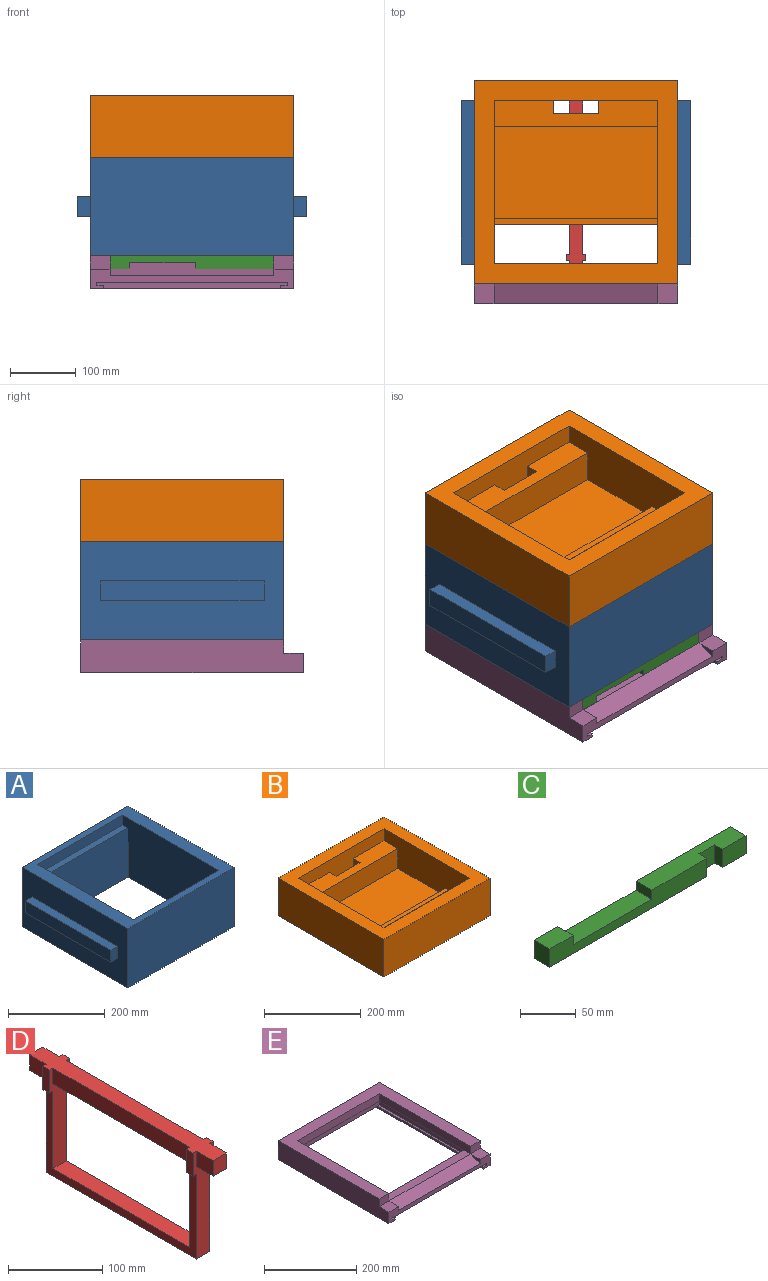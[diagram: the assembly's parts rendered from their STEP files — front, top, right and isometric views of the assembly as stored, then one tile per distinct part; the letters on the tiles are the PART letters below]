
ASSEMBLY  parts=5 mates=4
PART A: 24 faces, bbox 350x310x150 mm
  f0: plane 310x150mm, normal (1,0,0), area 39000mm2, adj f3,f4,f8,f9,f19,f20,f21,f22
  f1: plane 250x125mm, normal (0,1,0), area 31250mm2, adj f5,f6,f9,f12
  f2: plane 250x125mm, normal (0,-1,0), area 31250mm2, adj f5,f6,f9,f11
  f3: plane 310x150mm, normal (0,-1,0), area 46500mm2, adj f0,f7,f8,f9
  f4: plane 310x150mm, normal (0,1,0), area 46500mm2, adj f0,f7,f8,f9
  f5: plane 280x150mm, normal (-1,0,0), area 38250mm2, adj f1,f2,f8,f9,f10,f11,f12,f13
  f6: plane 280x150mm, normal (1,0,0), area 38250mm2, adj f1,f2,f8,f9,f10,f11,f12,f13
  f7: plane 310x150mm, normal (-1,0,0), area 39000mm2, adj f3,f4,f8,f9,f14,f15,f16,f17
  f8: plane 310x310mm, normal (0,0,1), area 26100mm2, adj f0,f3,f4,f5,f6,f7,f10,f13
  f9: plane 310x310mm, normal (0,0,-1), area 33600mm2, adj f0,f1,f2,f3,f4,f5,f6,f7
  f10: plane 250x25mm, normal (0,-1,0), area 6250mm2, adj f5,f6,f8,f11
  f11: plane 250x15mm, normal (0,0,1), area 3750mm2, adj f2,f5,f6,f10
  f12: plane 250x15mm, normal (0,0,1), area 3750mm2, adj f1,f5,f6,f13
  f13: plane 250x25mm, normal (0,1,0), area 6250mm2, adj f5,f6,f8,f12
  f14: plane 30x20mm, normal (0,-1,0), area 600mm2, adj f7,f15,f17,f18
  f15: plane 250x20mm, normal (0,0,1), area 5000mm2, adj f7,f14,f16,f18
  f16: plane 30x20mm, normal (0,1,0), area 600mm2, adj f7,f15,f17,f18
  f17: plane 250x20mm, normal (0,0,-1), area 5000mm2, adj f7,f14,f16,f18
  f18: plane 250x30mm, normal (-1,0,0), area 7500mm2, adj f14,f15,f16,f17
  f19: plane 30x20mm, normal (0,1,0), area 600mm2, adj f0,f20,f22,f23
  f20: plane 250x20mm, normal (0,0,1), area 5000mm2, adj f0,f19,f21,f23
  f21: plane 30x20mm, normal (0,-1,0), area 600mm2, adj f0,f20,f22,f23
  f22: plane 250x20mm, normal (0,0,-1), area 5000mm2, adj f0,f19,f21,f23
  f23: plane 250x30mm, normal (1,0,0), area 7500mm2, adj f19,f20,f21,f22
PART B: 20 faces, bbox 310x310x95 mm
  f0: plane 250x190mm, normal (0,0,-1), area 46100mm2, adj f1,f6,f8,f11,f12,f14,f16
  f1: plane 250x95mm, normal (1,0,0), area 19650mm2, adj f0,f2,f7,f8,f10,f13,f15,f16
  f2: plane 250x140mm, normal (0,0,1), area 35000mm2, adj f1,f6,f13,f17
  f3: plane 310x95mm, normal (0,-1,0), area 29450mm2, adj f4,f9,f10,f19
  f4: plane 310x95mm, normal (1,0,0), area 29450mm2, adj f3,f5,f10,f19
  f5: plane 310x95mm, normal (0,1,0), area 29450mm2, adj f4,f9,f10,f19
  f6: plane 250x95mm, normal (-1,0,0), area 19650mm2, adj f0,f2,f7,f8,f10,f13,f15,f16
  f7: plane 250x95mm, normal (0,1,0), area 23750mm2, adj f1,f6,f10,f19
  f8: plane 250x95mm, normal (0,-1,0), area 12950mm2, adj f0,f1,f6,f10,f12,f14,f15,f19
  f9: plane 310x95mm, normal (-1,0,0), area 29450mm2, adj f3,f5,f10,f19
  f10: plane 310x310mm, normal (0,0,1), area 33600mm2, adj f1,f3,f4,f5,f6,f7,f8,f9
  f11: plane 70x60mm, normal (0,1,0), area 4200mm2, adj f0,f12,f14,f15
  f12: plane 60x20mm, normal (-1,0,0), area 1200mm2, adj f0,f8,f11,f15
  f13: plane 250x50mm, normal (0,-1,0), area 12500mm2, adj f1,f2,f6,f15
  f14: plane 60x20mm, normal (1,0,0), area 1200mm2, adj f0,f8,f11,f15
  f15: plane 250x40mm, normal (0,0,1), area 8600mm2, adj f1,f6,f8,f11,f12,f13,f14
  f16: plane 250x30mm, normal (0,-1,0), area 7500mm2, adj f0,f1,f6,f18
  f17: plane 250x20mm, normal (0,1,0), area 5000mm2, adj f1,f2,f6,f18
  f18: plane 250x10mm, normal (0,0,1), area 2500mm2, adj f1,f6,f16,f17
  f19: plane 310x310mm, normal (0,0,-1), area 33600mm2, adj f1,f3,f4,f5,f6,f7,f8,f9
PART C: 14 faces, bbox 250x20x20 mm
  f0: plane 120x20mm, normal (0,0,1), area 2200mm2, adj f1,f2,f4,f5,f8,f9,f10,f11
  f1: plane 200x20mm, normal (0,-1,0), area 3000mm2, adj f0,f3,f6,f7,f8,f11,f12,f13
  f2: plane 30x20mm, normal (0,-1,0), area 600mm2, adj f0,f4,f7,f9
  f3: plane 30x20mm, normal (0,0,1), area 600mm2, adj f1,f5,f6,f12
  f4: plane 20x20mm, normal (1,0,0), area 400mm2, adj f0,f2,f5,f7
  f5: plane 250x20mm, normal (0,1,0), area 4000mm2, adj f0,f3,f4,f6,f7,f11,f12,f13
  f6: plane 20x20mm, normal (-1,0,0), area 400mm2, adj f1,f3,f5,f7
  f7: plane 250x20mm, normal (0,0,-1), area 4800mm2, adj f1,f2,f4,f5,f6,f8,f9,f10
  f8: plane 20x10mm, normal (1,0,0), area 200mm2, adj f0,f1,f7,f10
  f9: plane 20x10mm, normal (-1,0,0), area 200mm2, adj f0,f2,f7,f10
  f10: plane 20x20mm, normal (0,-1,0), area 400mm2, adj f0,f7,f8,f9
  f11: plane 20x10mm, normal (-1,0,0), area 200mm2, adj f0,f1,f5,f13
  f12: plane 20x10mm, normal (1,0,0), area 200mm2, adj f1,f3,f5,f13
  f13: plane 100x20mm, normal (0,0,1), area 2000mm2, adj f1,f5,f11,f12
PART D: 32 faces, bbox 30x275x140 mm
  f0: plane 205x7.5mm, normal (0,0,-1), area 1537.5mm2, adj f1,f3,f14,f30
  f1: plane 130x30mm, normal (0,-1,0), area 2475mm2, adj f0,f2,f3,f4,f12,f16,f21,f24
  f2: plane 205x20mm, normal (1,0,0), area 4100mm2, adj f1,f4,f12,f14
  f3: plane 205x20mm, normal (-1,0,0), area 4100mm2, adj f0,f1,f12,f14
  f4: plane 205x7.5mm, normal (0,0,-1), area 1537.5mm2, adj f1,f2,f14,f29
  f5: plane 25x20mm, normal (1,0,0), area 500mm2, adj f7,f10,f12,f23
  f6: plane 25x20mm, normal (-1,0,0), area 500mm2, adj f7,f10,f12,f23
  f7: plane 25x20mm, normal (0,0,-1), area 500mm2, adj f5,f6,f10,f23
  f8: plane 20x20mm, normal (0,-1,0), area 400mm2, adj f9,f11,f12,f13
  f9: plane 25x20mm, normal (1,0,0), area 500mm2, adj f8,f12,f13,f15
  f10: plane 20x20mm, normal (0,1,0), area 400mm2, adj f5,f6,f7,f12
  f11: plane 25x20mm, normal (-1,0,0), area 500mm2, adj f8,f12,f13,f15
  f12: plane 275x30mm, normal (0,0,1), area 5700mm2, adj f1,f2,f3,f5,f6,f8,f9,f10
  f13: plane 25x20mm, normal (0,0,-1), area 500mm2, adj f8,f9,f11,f15
  f14: plane 130x30mm, normal (0,1,0), area 2475mm2, adj f0,f2,f3,f4,f12,f16,f17,f18
  f15: plane 140x30mm, normal (0,-1,0), area 2700mm2, adj f9,f11,f12,f13,f16,f17,f18,f19
  f16: plane 225x110mm, normal (1,0,0), area 4250mm2, adj f1,f14,f15,f17,f22,f23,f24,f28
  f17: plane 10x5mm, normal (0,0,-1), area 50mm2, adj f14,f15,f16,f18
  f18: plane 30x10mm, normal (1,0,0), area 300mm2, adj f12,f14,f15,f17
  f19: plane 30x10mm, normal (-1,0,0), area 300mm2, adj f12,f14,f15,f20
  f20: plane 10x5mm, normal (0,0,-1), area 50mm2, adj f14,f15,f19,f21
  f21: plane 225x110mm, normal (-1,0,0), area 4250mm2, adj f1,f14,f15,f20,f22,f23,f25,f28
  f22: plane 225x20mm, normal (0,0,-1), area 4500mm2, adj f15,f16,f21,f23
  f23: plane 140x30mm, normal (0,1,0), area 2700mm2, adj f5,f6,f7,f12,f16,f21,f22,f24
  f24: plane 10x5mm, normal (0,0,-1), area 50mm2, adj f1,f16,f23,f27
  f25: plane 10x5mm, normal (0,0,-1), area 50mm2, adj f1,f21,f23,f26
  f26: plane 30x10mm, normal (-1,0,0), area 300mm2, adj f1,f12,f23,f25
  f27: plane 30x10mm, normal (1,0,0), area 300mm2, adj f1,f12,f23,f24
  f28: plane 205x20mm, normal (0,0,1), area 4100mm2, adj f1,f14,f16,f21
  f29: plane 205x5mm, normal (1,0,0), area 1025mm2, adj f1,f4,f14,f31
  f30: plane 205x5mm, normal (-1,0,0), area 1025mm2, adj f0,f1,f14,f31
  f31: plane 205x5mm, normal (0,0,-1), area 1025mm2, adj f1,f14,f29,f30
PART E: 30 faces, bbox 310x340x50 mm
  f0: plane 310x30mm, normal (0,-1,0), area 4000mm2, adj f1,f4,f8,f9,f15,f17,f19,f20
  f1: plane 330x5mm, normal (-1,0,0), area 1650mm2, adj f0,f23,f27,f29
  f2: plane 270x20mm, normal (-1,0,0), area 5400mm2, adj f3,f6,f22,f24
  f3: plane 270x20mm, normal (0,1,0), area 5400mm2, adj f2,f5,f7,f22,f24
  f4: plane 330x5mm, normal (1,0,0), area 1650mm2, adj f0,f23,f26,f29
  f5: plane 270x20mm, normal (1,0,0), area 5400mm2, adj f3,f6,f22,f24
  f6: plane 270x20mm, normal (0,-1,0), area 5400mm2, adj f2,f5,f22,f24
  f7: plane 250x20mm, normal (0,0,1), area 5000mm2, adj f3,f11,f13,f19
  f8: plane 30x30mm, normal (0,0,1), area 900mm2, adj f0,f14,f15,f20
  f9: plane 30x30mm, normal (0,0,1), area 900mm2, adj f0,f10,f17,f21
  f10: plane 30x20mm, normal (0,-1,0), area 600mm2, adj f9,f11,f17,f18
  f11: plane 280x20mm, normal (1,0,0), area 5600mm2, adj f7,f10,f12,f18,f22
  f12: plane 250x20mm, normal (0,-1,0), area 5000mm2, adj f11,f13,f18,f22
  f13: plane 280x20mm, normal (-1,0,0), area 5600mm2, adj f7,f12,f14,f18,f22
  f14: plane 30x20mm, normal (0,-1,0), area 600mm2, adj f8,f13,f15,f18
  f15: plane 340x50mm, normal (1,0,0), area 16400mm2, adj f0,f8,f14,f16,f18,f23
  f16: plane 310x50mm, normal (0,1,0), area 15500mm2, adj f15,f17,f18,f23
  f17: plane 340x50mm, normal (-1,0,0), area 16400mm2, adj f0,f9,f10,f16,f18,f23
  f18: plane 310x310mm, normal (0,0,1), area 26100mm2, adj f10,f11,f12,f13,f14,f15,f16,f17
  f19: plane 250x30mm, normal (0,-0.32,0.95), area 7905.7mm2, adj f0,f7,f20,f21
  f20: plane 30x10mm, normal (-1,0,0), area 150mm2, adj f0,f8,f19
  f21: plane 30x10mm, normal (1,0,0), area 150mm2, adj f0,f9,f19
  f22: plane 270x270mm, normal (0,0,-1), area 7900mm2, adj f2,f3,f5,f6,f11,f12,f13
  f23: plane 340x310mm, normal (0,0,-1), area 16300mm2, adj f0,f1,f4,f15,f16,f17,f29
  f24: plane 330x290mm, normal (0,0,-1), area 22800mm2, adj f0,f2,f3,f5,f6,f25,f28,f29
  f25: plane 330x5mm, normal (1,0,0), area 1650mm2, adj f0,f24,f26,f29
  f26: plane 330x10mm, normal (0,0,1), area 3300mm2, adj f0,f4,f25,f29
  f27: plane 330x10mm, normal (0,0,1), area 3300mm2, adj f0,f1,f28,f29
  f28: plane 330x5mm, normal (-1,0,0), area 1650mm2, adj f0,f24,f27,f29
  f29: plane 290x10mm, normal (0,-1,0), area 2800mm2, adj f1,f4,f23,f24,f25,f26,f27,f28
PLACE A t=(356.47,26.2,-100.56)mm
PLACE B t=(356.47,26.2,-20.56)mm
PLACE C rot(axis=(-1,0,0),180deg) t=(356.47,-118.8,-175.56)mm
PLACE D t=(356.47,18.7,-40.56)mm
PLACE E t=(356.47,26.2,-205.56)mm
MATE fastened B.f19 <-> A.f8  axis (0,0,-1) through (201.47,26.2,-25.56)mm
MATE fastened E.f11 <-> C.f6  axis (1,0,0) through (231.47,-128.8,-185.56)mm
MATE fastened A.f12 <-> D.f13  axis (0,0,1) through (356.47,-106.3,-50.56)mm
MATE fastened A.f9 <-> E.f18  axis (0,0,-1) through (511.47,-128.8,-175.56)mm
